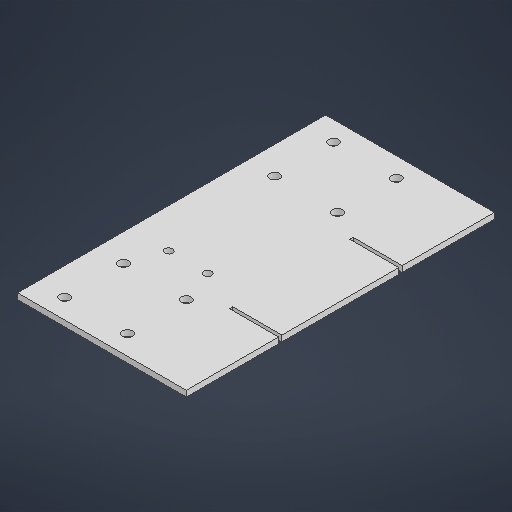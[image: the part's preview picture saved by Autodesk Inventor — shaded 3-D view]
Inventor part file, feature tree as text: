
AUTODESK INVENTOR PART (.ipt)
format: ipt  version: 2025.1 (Build 291241000, 241)  size: 458,752 bytes
history: native  units: mm
features: hole x2, sketch x1, extrude x1
ambient origin geometry x8: Origin, YZ Plane, XZ Plane, XY Plane, X Axis, Y Axis, Z Axis, Center Point
bodies: Solid1 (feature_tree)
feature tree (4):
  sketch  "Sketch1"  dims[d0=86.0mm d1=157.0mm d2=32.0mm d3=30.0mm d4=14.0mm d5=10.0mm d6=32.0mm d7=30.0mm d8=10.0mm d9=14.0mm d10=1.7mm d11=1.7mm d13=47.0mm d15=25.0mm d16=47.0mm d17=3.0mm d18=0.0mm d19=5.0mm d20=6.0mm d21=4.0mm d22=2.0mm d23=90.0deg d24=8.0mm d25=20.594885mm d26=19.9mm d27=20.0mm d28=57.0mm d29=4.0mm d30=6.0mm d31=4.0mm d32=2.0mm d33=90.0deg d34=8.0mm d35=20.594885mm]
  extrude  "Extrusion1"  Depth=157.0mm
  hole  "Hole1"  [1 undecoded]
  hole  "Hole2"  [1 undecoded]
note: 2 required parameter values undecoded (feature->parameter linkage not recoverable at this tier; creation-order binding heuristic only, values carry confidence <= 0.55)
